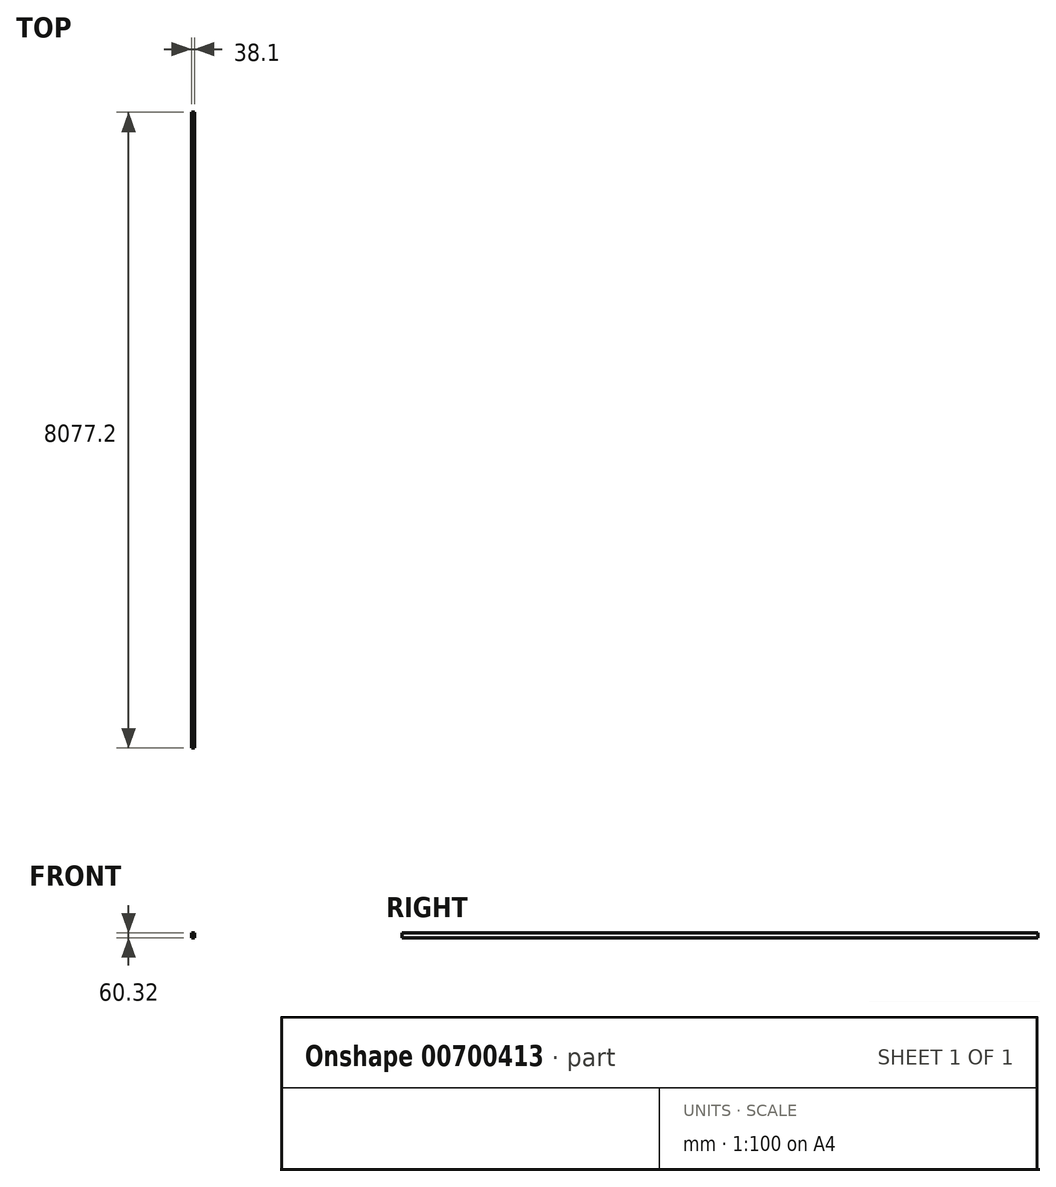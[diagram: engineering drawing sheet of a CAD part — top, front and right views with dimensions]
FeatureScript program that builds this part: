
annotation { "Feature Type Name" : "Feature", "Feature Type Description" : "" }
export const myFeature = defineFeature(function(context is Context, id is Id, definition is map)
    precondition{}
    {
        {
            var Q0;
            Q0=qCreatedBy(makeId("Front.planeOp"),FACE);
            var sketch = newSketch(context, id + "F0", { "sketchPlane" : qUnion([Q0])});
            skLineSegment(sketch, "E0.bottom", {"start": v(-19.05, 30.16) * mm, "end": v(19.05, 30.16) * mm});
            skLineSegment(sketch, "E0.top", {"start": v(-19.05, -30.16) * mm, "end": v(19.05, -30.16) * mm});
            skLineSegment(sketch, "E0.left", {"start": v(-19.05, 30.16) * mm, "end": v(-19.05, -30.16) * mm});
            skLineSegment(sketch, "E0.right", {"start": v(19.05, 30.16) * mm, "end": v(19.05, -30.16) * mm});
            skLineSegment(sketch, "E1", {"start": v(-19.05, 30.16) * mm, "end": v(19.05, -30.16) * mm, "construction": true});
            skSolve(sketch);
        }
        {
            var Q0;
            Q0 = qSketchRegion(id + "F0", true);
            extrude(context, id + "F1", {"entities" : qUnion([Q0]), "endBound" : BoundingType.SYMMETRIC, "depth" : 8077.2 * mm, "offsetDistance" : 25.4 * mm});
        }
    });
